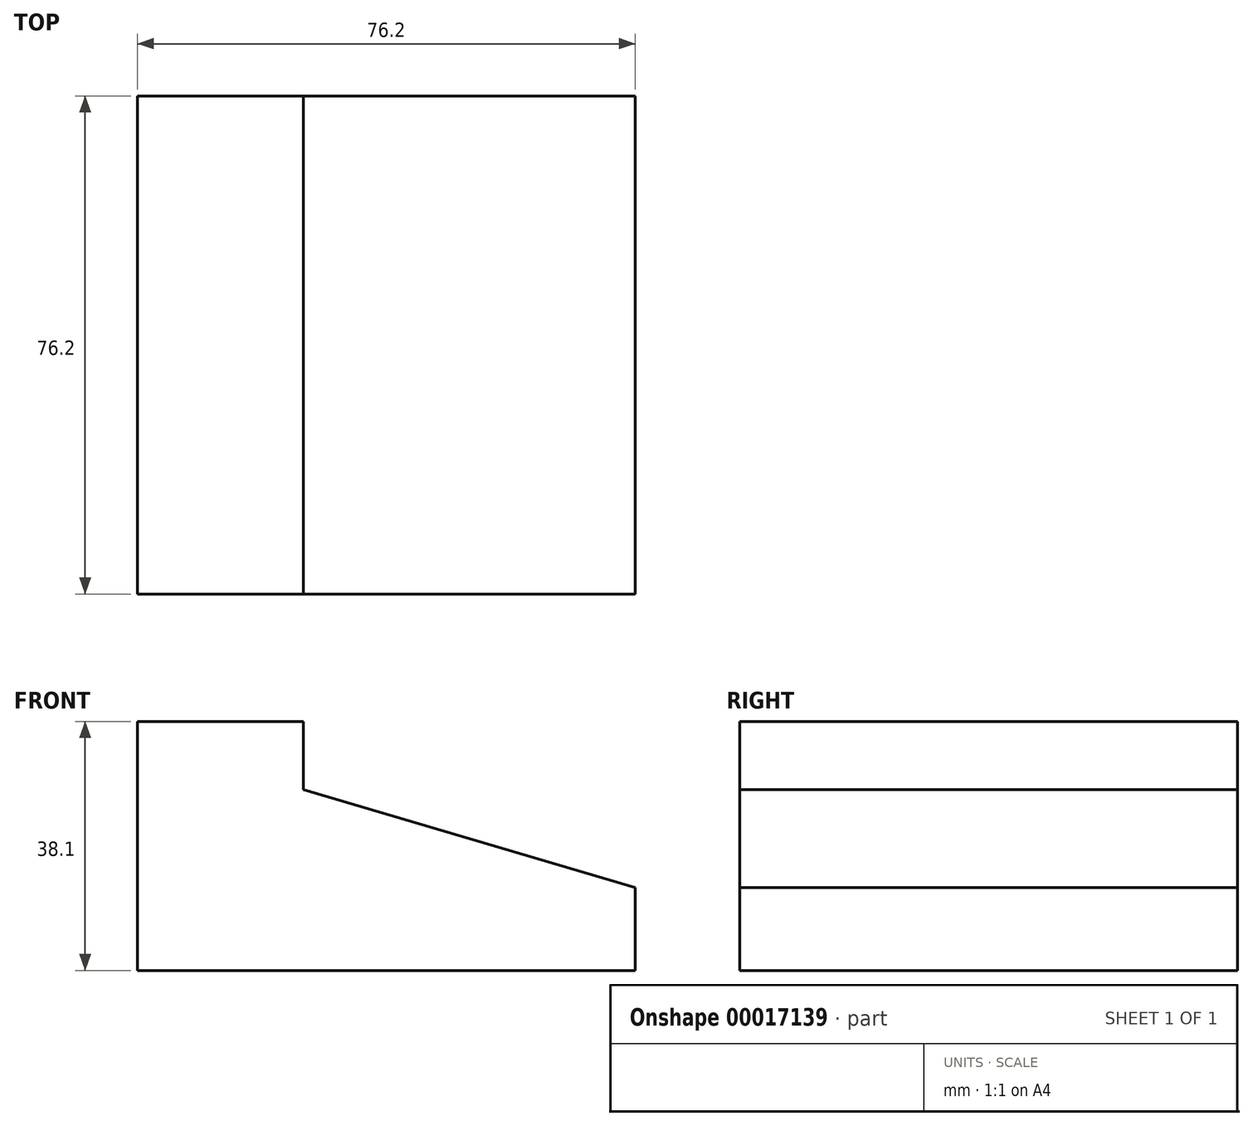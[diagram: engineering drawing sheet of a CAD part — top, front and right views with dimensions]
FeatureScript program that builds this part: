
annotation { "Feature Type Name" : "Feature", "Feature Type Description" : "" }
export const myFeature = defineFeature(function(context is Context, id is Id, definition is map)
    precondition{}
    {
        {
            var Q0;
            Q0=qCreatedBy(makeId("Front.planeOp"),FACE);
            var sketch = newSketch(context, id + "F0", { "sketchPlane" : qUnion([Q0])});
            skLineSegment(sketch, "E0", {"start": v(-42.69, -4.65) * mm, "end": v(-42.69, -42.75) * mm});
            skLineSegment(sketch, "E1", {"start": v(-42.69, -42.75) * mm, "end": v(33.51, -42.75) * mm});
            skLineSegment(sketch, "E2", {"start": v(33.51, -42.75) * mm, "end": v(33.51, -30.05) * mm});
            skLineSegment(sketch, "E3", {"start": v(33.51, -30.05) * mm, "end": v(-17.29, -15.06) * mm});
            skLineSegment(sketch, "E4", {"start": v(-17.29, -15.06) * mm, "end": v(-17.29, -2.36) * mm});
            skLineSegment(sketch, "E5", {"start": v(-42.69, -4.65) * mm, "end": v(-17.29, -4.65) * mm});
            skSolve(sketch);
        }
        {
            var Q0;
            Q0 = qSketchRegion(id + "F0", true);
            extrude(context, id + "F1", {"entities" : qUnion([Q0]), "depth" : 76.2 * mm});
        }
    });
